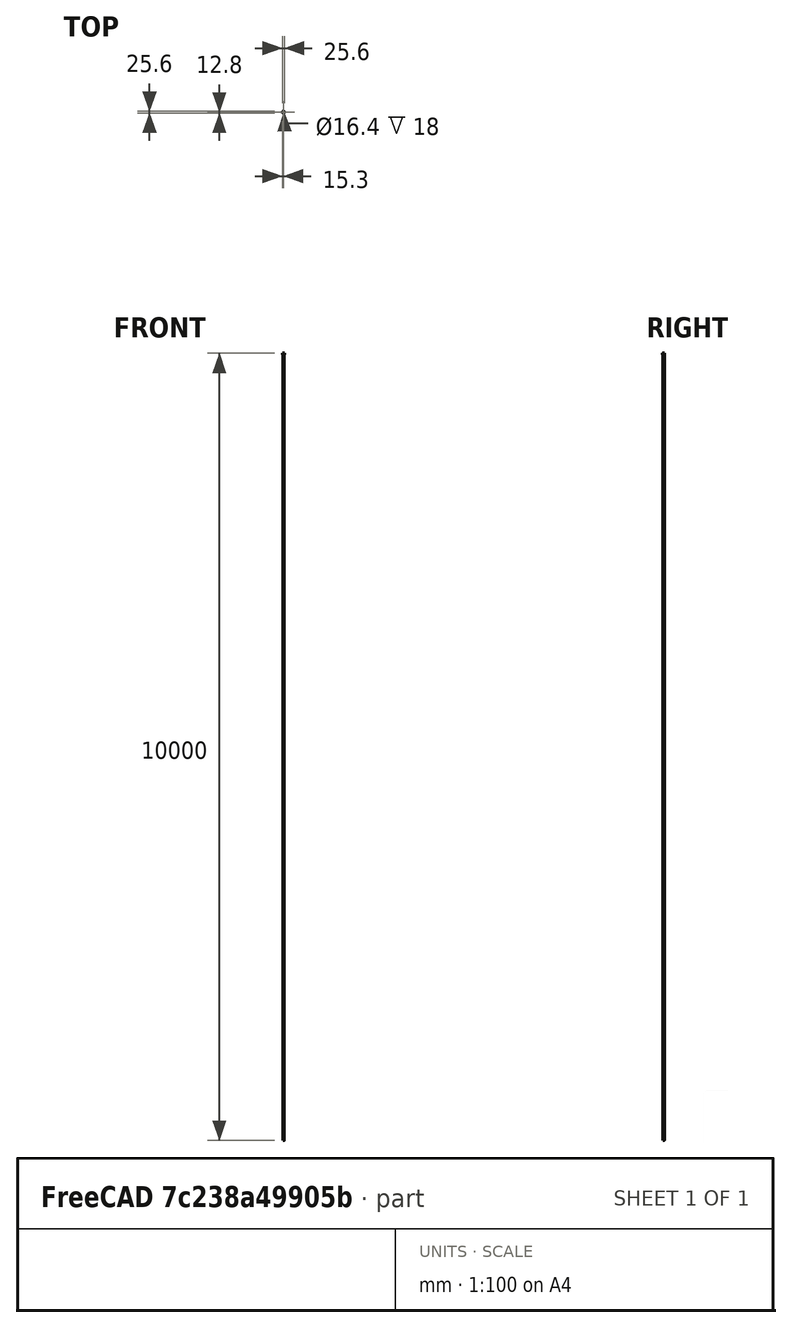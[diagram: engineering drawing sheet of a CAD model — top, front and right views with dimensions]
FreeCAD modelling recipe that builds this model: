
FCSTD DOCUMENT  (FreeCAD 0.16R)
Label: LeverEcc24-16-16
License: All rights reserved
LicenseURL: http://en.wikipedia.org/wiki/All_rights_reserved
objects: Sketcher::SketchObject×5, PartDesign::Pad×3, PartDesign::Pocket×2, PartDesign::Chamfer×1, Mesh::Feature×1
note: 16 computed .brp shape members not serialized (recipe doc carries the construction recipe); baked Part::Feature solids carry a one-line shape summary decoded from their .brp

FEATURE [Sketcher::SketchObject] Sketch
  sketch-geometry (1):
    g0: Circle CenterX=0 CenterY=0 CenterZ=0 NormalX=0 NormalY=0 NormalZ=1 Radius=11.8
  constraints (2):
    c: Radius(g0) = 11.8
    c: Coincident(g0,g-1)
FEATURE [PartDesign::Pad] Pad
  Length = 16
  Length2 = 100
  Sketch = -> Sketch
  Type = 0
FEATURE [Sketcher::SketchObject] Sketch001
  Placement = pos=(0,0,16) rot=(0,0,1;0rad)
  Support = -> Pad [Face3]
  sketch-geometry (1):
    g0: Circle CenterX=0 CenterY=0 CenterZ=0 NormalX=0 NormalY=0 NormalZ=1 Radius=12.8
  constraints (2):
    c: Radius(g0) = 12.8
    c: Coincident(g0,g-1)
FEATURE [PartDesign::Pad] Pad001
  Length = 1
  Length2 = 100
  Sketch = -> Sketch001
  Type = 0
FEATURE [Sketcher::SketchObject] Sketch002
  Placement = pos=(0,0,0) rot=(1,0,0;3.14159rad)
  Support = -> Pad001 [Face1]
  sketch-geometry (1):
    g0: Circle CenterX=0 CenterY=0 CenterZ=0 NormalX=0 NormalY=0 NormalZ=1 Radius=12.8
  constraints (2):
    c: Radius(g0) = 12.8
    c: Coincident(g0,g-1)
FEATURE [PartDesign::Pad] Pad002
  Length = 1
  Length2 = 100
  Sketch = -> Sketch002
  Type = 0
FEATURE [Sketcher::SketchObject] Sketch003
  Placement = pos=(0,0,17) rot=(0,0,1;0rad)
  Support = -> Pad002 [Face4]
  sketch-geometry (1):
    g0: Circle CenterX=2.5 CenterY=0 CenterZ=0 NormalX=0 NormalY=0 NormalZ=1 Radius=8.2
  constraints (3):
    c: Radius(g0) = 8.2
    c: PointOnObject(g0,g-1)
    c: DistanceX(g0) = 2.5
FEATURE [PartDesign::Pocket] Pocket
  Length = 5
  Sketch = -> Sketch003
  Type = 1
FEATURE [Sketcher::SketchObject] Sketch004
  Placement = pos=(0,0,-1) rot=(1,0,0;3.14159rad)
  Support = -> Pocket [Face8]
  sketch-geometry (4):
    g0: LineSegment StartX=-35 StartY=0.5 StartZ=0 EndX=35 EndY=0.5 EndZ=0
    g1: LineSegment StartX=35 StartY=0.5 StartZ=0 EndX=35 EndY=-0.5 EndZ=0
    g2: LineSegment StartX=35 StartY=-0.5 StartZ=0 EndX=-35 EndY=-0.5 EndZ=0
    g3: LineSegment StartX=-35 StartY=-0.5 StartZ=0 EndX=-35 EndY=0.5 EndZ=0
  constraints (12):
    c: Coincident(g0,g1)
    c: Coincident(g1,g2)
    c: Coincident(g2,g3)
    c: Coincident(g3,g0)
    c: Horizontal(g0)
    c: Horizontal(g2)
    c: Vertical(g1)
    c: Vertical(g3)
    c: Symmetric(g1,g0,g-1)
    c: Distance(g1) = 1
    c: Symmetric(g1,g2,g-2)
    c: Distance(g0) = 70
FEATURE [PartDesign::Pocket] Pocket001
  Length = 17.9
  Sketch = -> Sketch004
  Type = 0
FEATURE [PartDesign::Chamfer] Chamfer
  Base = -> Pocket001 [Edge7,Edge1,Edge51,Edge54]
  Size = 0.8
FEATURE [Mesh::Feature] Mesh  label="Chamfer (Meshed)"
